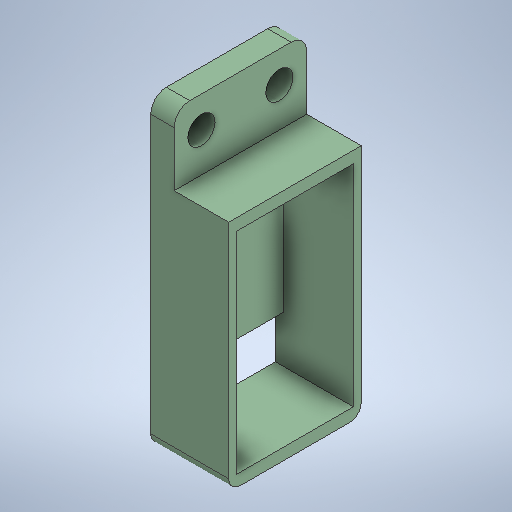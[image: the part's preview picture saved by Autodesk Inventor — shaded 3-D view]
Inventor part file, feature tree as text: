
AUTODESK INVENTOR PART (.ipt)
format: ipt  version: 2025 (Build 290162000, 162)  size: 619,008 bytes
history: native  units: mm
features: extrude x5, sketch x5, fillet x2
ambient origin geometry x8: Origin, YZ Plane, XZ Plane, XY Plane, X Axis, Y Axis, Z Axis, Center Point
bodies: Solide1 (feature_tree)
feature tree (12):
  extrude  "Extrusion1"  Depth=30.0mm
  extrude  "Extrusion2"  Depth=17.0mm
  extrude  "Extrusion3"  Depth=10.0mm TaperAngle=0.0deg
  extrude  "Extrusion4"  Depth=27.0mm
  extrude  "Extrusion5"  Depth=15.0mm
  fillet  "Congé1"  Radius=9.0mm
  fillet  "Congé2"  Radius=6.0mm
  sketch  "Esquisse1"
  sketch  "Esquisse2"
  sketch  "Esquisse3"
  sketch  "Esquisse4"
  sketch  "Esquisse5"
